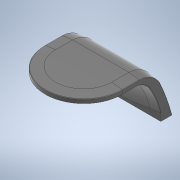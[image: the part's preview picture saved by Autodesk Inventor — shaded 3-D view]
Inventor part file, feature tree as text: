
AUTODESK INVENTOR PART (.ipt)
format: ipt  version: 2020 (Build 240168000, 168)  size: 7,272,960 bytes
history: native  units: in
note: dims shown in document units (in); Inventor stores cm internally (conversion verified against a paired STEP export)
features: chamfer x7, other x5, revolve x3, extrude x2, sketch x2, split x1, sweep x1
ambient origin geometry x8: Origin, YZ Plane, XZ Plane, XY Plane, X Axis, Y Axis, Z Axis, Center Point
bodies: Body1 (feature_tree)
feature tree (21):
  other  "ProfileTop"
  other  "ProfileSide"
  other  "XY_Project"
  other  "ProfileBack"
  revolve  "RevolvePlane"  [1 undecoded]
  revolve  "RevolveSketch"  [1 undecoded]
  extrude  "Extrusion5"  Depth=3.715in
  extrude  "Extrusion6"  Depth=30.973in
  split  "Split1"
  revolve  "Revolution1"  [1 undecoded]
  chamfer  "Chamfer4"  Distance=5.4528in
  chamfer  "Chamfer5"  Distance=5.4528in
  chamfer  "Chamfer6"  Distance=2.937in
  chamfer  "Chamfer7"  Distance=16.7023in
  sweep  "Sweep1"
  chamfer  "Chamfer8"  Distance=2.937in
  chamfer  "Chamfer9"  Distance=1.8504in
  chamfer  "Chamfer10"  Distance=7.4452in
  other  "Image8"
  sketch  "Sketch9"  dims[d98=7.874in d109=2.278in d110=12.4228in d111=3.715in d112=30.973in d142=7.874in d155=5.4528in d158=5.4528in d159=2.937in d160=16.7023in d161=16.7023in d162=2.937in d170=1.8504in d171=7.4452in d172=5.4724in d173=0.0in d174=4.9332in d175=5.4231in d176=1.7487in d177=4.8557in d178=1.8083in d179=1.6341in d180=0.8398in d181=0.0in d187=0.5906in d188=0.1969in d189=0.1969in d272=29.8893in d278=8.1496in d279=1.2598in d280=10.9449in d281=6.8898in d282=1.2598in d283=5.4724in d284=5.4724in d285=8.1496in d288=15.748in d289=0.0in d290=15.748in d291=0.0in d346=180.0deg d347=1.4961in d348=1.4961in d349=5.4724in d350=0.1969in d351=1.4961in d352=45.0deg d353=0.1969in d354=1.4961in d355=45.0deg d356=0.1969in d357=1.4961in d358=45.0deg d359=0.1969in d360=1.4961in d361=45.0deg d362=0.0in d363=0.0in d364=0.1969in d365=1.4961in d366=45.0deg d367=0.1969in d368=1.4961in d369=45.0deg d370=0.0591in d371=1.4961in d372=45.0deg d163=0.0197in d164=0.0344in d165=0.0197in d166=0.0344in]
  sketch  "3D Sketch1"
note: 3 required parameter values undecoded (feature->parameter linkage not recoverable at this tier; creation-order binding heuristic only, values carry confidence <= 0.55)
